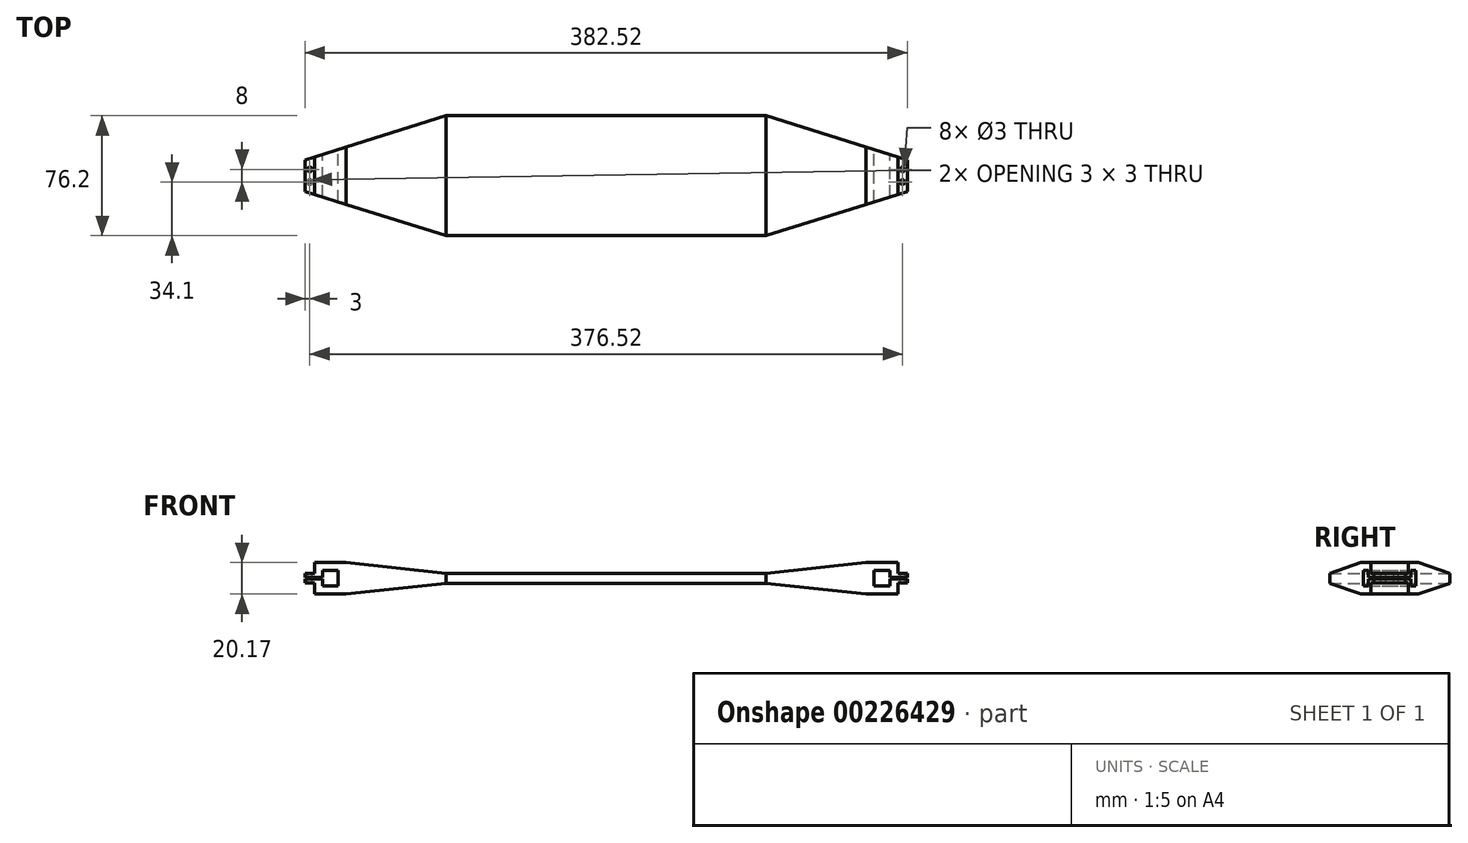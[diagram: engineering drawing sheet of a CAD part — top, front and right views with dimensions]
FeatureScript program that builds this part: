
annotation { "Feature Type Name" : "Feature", "Feature Type Description" : "" }
export const myFeature = defineFeature(function(context is Context, id is Id, definition is map)
    precondition{}
    {
        {
            var Q0;
            Q0=qCreatedBy(makeId("Front.planeOp"),FACE);
            var sketch = newSketch(context, id + "F0", { "sketchPlane" : qUnion([Q0])});
            skLineSegment(sketch, "E0.bottom", {"start": v(-180.18, 8.18) * mm, "end": v(-170.18, 8.18) * mm});
            skLineSegment(sketch, "E0.top", {"start": v(-180.18, -1.83) * mm, "end": v(-170.18, -1.83) * mm});
            skLineSegment(sketch, "E0.right", {"start": v(-170.18, 8.18) * mm, "end": v(-170.18, -1.83) * mm});
            skLineSegment(sketch, "E1.bottom", {"start": v(-165.1, -6.9) * mm, "end": v(-185.26, -6.9) * mm});
            skLineSegment(sketch, "E1.top", {"start": v(-165.1, 13.25) * mm, "end": v(-185.26, 13.25) * mm});
            skLineSegment(sketch, "E1.left", {"start": v(-165.1, -6.9) * mm, "end": v(-165.1, 13.25) * mm});
            skLineSegment(sketch, "E1.right", {"start": v(-185.26, -6.9) * mm, "end": v(-185.26, 2.68) * mm});
            skPoint(sketch, "E1.middle", {"position": v(-175.18, 3.17) * mm});
            skLineSegment(sketch, "E2", {"start": v(-185.26, 13.25) * mm, "end": v(-180.18, 8.17) * mm, "construction": true});
            skLineSegment(sketch, "E3", {"start": v(-170.18, -1.83) * mm, "end": v(-165.1, -6.9) * mm, "construction": true});
            skLineSegment(sketch, "E4", {"start": v(-180.18, -1.82) * mm, "end": v(-185.26, -6.9) * mm, "construction": true});
            skLineSegment(sketch, "E5", {"start": v(-165.1, 6.35) * mm, "end": v(0, 6.35) * mm});
            skLineSegment(sketch, "E6", {"start": v(0, 0) * mm, "end": v(-165.1, 0) * mm});
            skLineSegment(sketch, "E7", {"start": v(-165.1, 13.25) * mm, "end": v(-101.6, 6.35) * mm});
            skLineSegment(sketch, "E8", {"start": v(-101.6, 6.35) * mm, "end": v(-101.6, 0) * mm});
            skLineSegment(sketch, "E9", {"start": v(-101.6, 0) * mm, "end": v(-165.1, -6.9) * mm});
            skLineSegment(sketch, "E10", {"start": v(0, 6.35) * mm, "end": v(0, 0) * mm});
            skLineSegment(sketch, "E11", {"start": v(-180.18, 3.68) * mm, "end": v(-185.26, 3.68) * mm});
            skLineSegment(sketch, "E12", {"start": v(-185.26, 2.68) * mm, "end": v(-180.18, 2.68) * mm});
            skPoint(sketch, "E13", {"position": v(-180.18, 3.17) * mm});
            skLineSegment(sketch, "E14.trimOffspring", {"start": v(-180.18, 2.68) * mm, "end": v(-180.18, -1.83) * mm});
            skLineSegment(sketch, "E15", {"start": v(-180.18, 3.67) * mm, "end": v(-180.18, 8.17) * mm});
            skLineSegment(sketch, "E16.trimOffspring", {"start": v(-185.26, 3.67) * mm, "end": v(-185.26, 13.25) * mm});
            skLineSegment(sketch, "E17", {"start": v(-185.26, 3.68) * mm, "end": v(-191.26, 3.68) * mm});
            skLineSegment(sketch, "E18", {"start": v(-191.26, 3.67) * mm, "end": v(-191.26, 6.22) * mm});
            skLineSegment(sketch, "E19", {"start": v(-191.26, 6.22) * mm, "end": v(-185.26, 6.22) * mm});
            skLineSegment(sketch, "E20", {"start": v(-185.26, 2.68) * mm, "end": v(-191.26, 2.68) * mm});
            skLineSegment(sketch, "E21", {"start": v(-191.26, 2.68) * mm, "end": v(-191.26, 0.13) * mm});
            skLineSegment(sketch, "E22", {"start": v(-191.26, 0.13) * mm, "end": v(-185.26, 0.13) * mm});
            skLineSegment(sketch, "E23.MirrorCS", {"start": v(180.18, 3.67) * mm, "end": v(180.18, 8.17) * mm});
            skLineSegment(sketch, "E24.MirrorCS", {"start": v(180.18, 2.68) * mm, "end": v(180.18, -1.83) * mm});
            skLineSegment(sketch, "E25.MirrorCS", {"start": v(191.26, 3.67) * mm, "end": v(191.26, 6.22) * mm});
            skLineSegment(sketch, "E26.MirrorCS", {"start": v(191.26, 2.67) * mm, "end": v(191.26, 0.13) * mm});
            skLineSegment(sketch, "E27.MirrorCS", {"start": v(180.18, 8.18) * mm, "end": v(170.18, 8.18) * mm});
            skLineSegment(sketch, "E28.MirrorCS", {"start": v(180.18, 3.68) * mm, "end": v(185.26, 3.68) * mm});
            skLineSegment(sketch, "E29.MirrorCS", {"start": v(185.26, 2.68) * mm, "end": v(180.18, 2.68) * mm});
            skLineSegment(sketch, "E30.MirrorCS", {"start": v(180.18, -1.82) * mm, "end": v(185.26, -6.9) * mm, "construction": true});
            skLineSegment(sketch, "E31.MirrorCS", {"start": v(185.26, 13.25) * mm, "end": v(180.18, 8.17) * mm, "construction": true});
            skLineSegment(sketch, "E32.MirrorCS", {"start": v(191.26, 6.22) * mm, "end": v(185.26, 6.22) * mm});
            skLineSegment(sketch, "E33.MirrorCS", {"start": v(185.26, -6.9) * mm, "end": v(185.26, 2.68) * mm});
            skLineSegment(sketch, "E34.MirrorCS", {"start": v(191.26, 0.13) * mm, "end": v(185.26, 0.13) * mm});
            skLineSegment(sketch, "E35.MirrorCS", {"start": v(170.18, 8.18) * mm, "end": v(170.18, -1.82) * mm});
            skLineSegment(sketch, "E36.MirrorCS", {"start": v(0, 0) * mm, "end": v(165.1, 0) * mm});
            skLineSegment(sketch, "E37.MirrorCS", {"start": v(180.18, -1.83) * mm, "end": v(170.18, -1.83) * mm});
            skPoint(sketch, "E38.MirrorP", {"position": v(175.18, 3.17) * mm});
            skPoint(sketch, "E39.MirrorP", {"position": v(180.18, 3.17) * mm});
            skLineSegment(sketch, "E40.MirrorCS", {"start": v(101.6, 6.35) * mm, "end": v(101.6, 0) * mm});
            skLineSegment(sketch, "E41.MirrorCS", {"start": v(165.1, 13.25) * mm, "end": v(185.26, 13.25) * mm});
            skLineSegment(sketch, "E42.MirrorCS", {"start": v(165.1, -6.9) * mm, "end": v(185.26, -6.9) * mm});
            skLineSegment(sketch, "E43.MirrorCS", {"start": v(185.26, 3.67) * mm, "end": v(185.26, 13.25) * mm});
            skLineSegment(sketch, "E44.MirrorCS", {"start": v(165.1, -6.9) * mm, "end": v(165.1, 13.25) * mm});
            skLineSegment(sketch, "E45.MirrorCS", {"start": v(165.1, 6.35) * mm, "end": v(0, 6.35) * mm});
            skLineSegment(sketch, "E46.MirrorCS", {"start": v(185.26, 3.68) * mm, "end": v(191.26, 3.68) * mm});
            skLineSegment(sketch, "E47.MirrorCS", {"start": v(101.6, 0) * mm, "end": v(165.1, -6.9) * mm});
            skLineSegment(sketch, "E48.MirrorCS", {"start": v(185.26, 2.68) * mm, "end": v(191.26, 2.68) * mm});
            skLineSegment(sketch, "E49.MirrorCS", {"start": v(170.18, -1.83) * mm, "end": v(165.1, -6.9) * mm, "construction": true});
            skLineSegment(sketch, "E50.MirrorCS", {"start": v(165.1, 13.25) * mm, "end": v(101.6, 6.35) * mm});
            skSolve(sketch);
        }
        {
            var Q0;
            Q0=qSketchRegion(id+"F0",true);
            extrude(context, id + "F1", {"entities" : qUnion([Q0]), "depth" : 76.2 * mm, "offsetDistance" : 25.4 * mm});
        }
        {
            var Q0;
            Q0=makeQuery(id+"F1.opExtrude","SWEPT_FACE",FACE,{"disambiguationData":[OSD([sQuery(id+"F0.wireOp",EDGE,"E5")])]});
            var sketch = newSketch(context, id + "F2", { "sketchPlane" : qUnion([Q0])});
            skLineSegment(sketch, "E51.bottom", {"start": v(-101.6, 0) * mm, "end": v(101.6, 0) * mm, "construction": true});
            skLineSegment(sketch, "E51.top", {"start": v(-101.6, -76.2) * mm, "end": v(101.6, -76.2) * mm, "construction": true});
            skLineSegment(sketch, "E51.left", {"start": v(-101.6, 0) * mm, "end": v(-101.6, -76.2) * mm, "construction": true});
            skLineSegment(sketch, "E51.right", {"start": v(101.6, 0) * mm, "end": v(101.6, -76.2) * mm, "construction": true});
            skLineSegment(sketch, "E52.bottom", {"start": v(-26, -12.1) * mm, "end": v(26, -12.1) * mm, "construction": true});
            skLineSegment(sketch, "E52.top", {"start": v(-26, -64.1) * mm, "end": v(26, -64.1) * mm, "construction": true});
            skLineSegment(sketch, "E52.left", {"start": v(-26, -12.1) * mm, "end": v(-26, -64.1) * mm, "construction": true});
            skLineSegment(sketch, "E52.right", {"start": v(26, -12.1) * mm, "end": v(26, -64.1) * mm, "construction": true});
            skLineSegment(sketch, "E53.bottom", {"start": v(-38.1, -9.52) * mm, "end": v(38.1, -9.52) * mm, "construction": true});
            skLineSegment(sketch, "E53.top", {"start": v(-38.1, -66.68) * mm, "end": v(38.1, -66.68) * mm, "construction": true});
            skLineSegment(sketch, "E53.left", {"start": v(-38.1, -9.52) * mm, "end": v(-38.1, -66.67) * mm, "construction": true});
            skLineSegment(sketch, "E53.right", {"start": v(38.1, -9.52) * mm, "end": v(38.1, -66.67) * mm, "construction": true});
            skLineSegment(sketch, "E54", {"start": v(0, -12.1) * mm, "end": v(0, 0) * mm, "construction": true});
            skLineSegment(sketch, "E55", {"start": v(26, -38.1) * mm, "end": v(101.6, -38.1) * mm, "construction": true});
            skLineSegment(sketch, "E56", {"start": v(0, -9.52) * mm, "end": v(0, 0) * mm});
            skLineSegment(sketch, "E57", {"start": v(38.1, -38.1) * mm, "end": v(101.6, -38.1) * mm, "construction": true});
            skCircle(sketch, "E58", {"center": v(-38.1, -9.52) * mm, "radius": 4.45 * mm});
            skCircle(sketch, "E59", {"center": v(38.1, -9.52) * mm, "radius": 4.45 * mm});
            skCircle(sketch, "E60", {"center": v(38.1, -66.67) * mm, "radius": 4.45 * mm});
            skCircle(sketch, "E61", {"center": v(-38.1, -66.67) * mm, "radius": 4.45 * mm});
            skCircle(sketch, "E62", {"center": v(-23, -15.1) * mm, "radius": 1.59 * mm});
            skCircle(sketch, "E63", {"center": v(23, -61.1) * mm, "radius": 1.59 * mm});
            skLineSegment(sketch, "E64", {"start": v(-23, -12.1) * mm, "end": v(-23, -64.1) * mm, "construction": true});
            skLineSegment(sketch, "E65", {"start": v(-26, -61.1) * mm, "end": v(26, -61.1) * mm, "construction": true});
            skLineSegment(sketch, "E66", {"start": v(23, -64.1) * mm, "end": v(23, -12.1) * mm, "construction": true});
            skLineSegment(sketch, "E67", {"start": v(26, -15.1) * mm, "end": v(-26, -15.1) * mm, "construction": true});
            skCircle(sketch, "E68", {"center": v(23, -15.1) * mm, "radius": 1.59 * mm});
            skCircle(sketch, "E69", {"center": v(-23, -61.1) * mm, "radius": 1.59 * mm});
            skSolve(sketch);
        }
        {
            var Q0;
            Q0=qSketchRegion(id+"F2",true);
            extrude(context, id + "F3", {"entities" : qUnion([Q0]), "operationType" : NewBodyOperationType.REMOVE, "oppositeDirection" : true, "depth" : 25.4 * mm, "offsetDistance" : 25.4 * mm});
        }
        {
            var Q0;
            Q0=makeQuery(id+"F1.opExtrude","SWEPT_FACE",FACE,{"disambiguationData":[OSD([sQuery(id+"F0.wireOp",EDGE,"E19")])]});
            var sketch = newSketch(context, id + "F4", { "sketchPlane" : qUnion([Q0])});
            skCircle(sketch, "E70", {"center": v(-188.26, -34.1) * mm, "radius": 1.5 * mm});
            skPoint(sketch, "E70.centerSnap0", {"position": v(-188.26, 0) * mm});
            skCircle(sketch, "E71", {"center": v(-188.26, -42.1) * mm, "radius": 1.5 * mm});
            skPoint(sketch, "E71.centerSnap0", {"position": v(-188.26, -76.2) * mm});
            skLineSegment(sketch, "E72", {"start": v(0, 0) * mm, "end": v(0, -76.82) * mm});
            skCircle(sketch, "E73.MirrorC", {"center": v(188.26, -42.1) * mm, "radius": 1.5 * mm});
            skCircle(sketch, "E74.MirrorC", {"center": v(188.26, -34.1) * mm, "radius": 1.5 * mm});
            skPoint(sketch, "E75.MirrorP", {"position": v(188.26, -76.2) * mm});
            skSolve(sketch);
        }
        {
            var Q0;
            Q0=qSketchRegion(id+"F4",true);
            extrude(context, id + "F5", {"entities" : qUnion([Q0]), "operationType" : NewBodyOperationType.REMOVE, "endBound" : BoundingType.THROUGH_ALL, "oppositeDirection" : true, "depth" : 25 * mm, "offsetDistance" : 25 * mm});
        }
        {
            var Q0;
            Q0=makeQuery(id+"F1.opExtrude","SWEPT_FACE",FACE,{"disambiguationData":[OSD([sQuery(id+"F0.wireOp",EDGE,"E1.top")])]});
            var sketch = newSketch(context, id + "F6", { "sketchPlane" : qUnion([Q0])});
            skPoint(sketch, "E76.0", {"position": v(-101.6, 0) * mm});
            skLineSegment(sketch, "E77", {"start": v(-101.6, 0) * mm, "end": v(-191.26, -28.1) * mm});
            skLineSegment(sketch, "E78.0", {"start": v(-191.26, -76.2) * mm, "end": v(-191.26, 0) * mm});
            skPoint(sketch, "E79", {"position": v(-191.26, -38.1) * mm});
            skLineSegment(sketch, "E80.MirrorCS", {"start": v(101.6, 0) * mm, "end": v(191.26, -28.1) * mm});
            skLineSegment(sketch, "E81", {"start": v(-191.26, -38.1) * mm, "end": v(196.24, -38.1) * mm});
            skLineSegment(sketch, "E82.MirrorCS", {"start": v(-101.6, -76.2) * mm, "end": v(-191.26, -48.1) * mm});
            skLineSegment(sketch, "E83.MirrorCS", {"start": v(101.6, -76.2) * mm, "end": v(191.26, -48.1) * mm});
            skLineSegment(sketch, "E84", {"start": v(-101.6, 0) * mm, "end": v(-191.26, 0) * mm});
            skLineSegment(sketch, "E85", {"start": v(-101.6, -76.2) * mm, "end": v(-191.26, -76.2) * mm});
            skLineSegment(sketch, "E86", {"start": v(101.6, -76.2) * mm, "end": v(191.26, -76.2) * mm});
            skLineSegment(sketch, "E87", {"start": v(191.26, -76.2) * mm, "end": v(191.26, -48.1) * mm});
            skLineSegment(sketch, "E88", {"start": v(191.26, -28.1) * mm, "end": v(191.26, 0) * mm});
            skLineSegment(sketch, "E89", {"start": v(191.26, 0) * mm, "end": v(101.6, 0) * mm});
            skSolve(sketch);
        }
        {
            var Q0;
            {var subQ0=sQuery(id+"F6.wireOp",EDGE,"E84");var subQ1=sQuery(id+"F6.wireOp",EDGE,"E77");var subQ2=makeQuery(id+"F6.imprint","INTERSECT",VERTEX,{"derivedFrom":[subQ1,subQ0]});Q0=makeQuery(id+"F6.imprint","IMPRINT",FACE,{"disambiguationData":[TD([[makeQuery(id+"F6.imprint","IMPRINT",EDGE,{"disambiguationData":[TD([[subQ2,-1.0]])],"derivedFrom":subQ1}),-1.0]])]});}
            var Q1;
            {var subQ0=sQuery(id+"F6.wireOp",EDGE,"E77");var subQ1=sQuery(id+"F0.wireOp",EDGE,"E1.top");var subQ4=makeQuery(id+"F1.opExtrude","SWEPT_EDGE",EDGE,{"disambiguationData":[OSD([subQ1,sQuery(id+"F0.wireOp",EDGE,"E16.trimOffspring")])]});var subQ5=makeQuery(id+"F6.imprint","INTERSECT",VERTEX,{"derivedFrom":[subQ4,subQ0]});Q1=makeQuery(id+"F6.imprint","IMPRINT",FACE,{"disambiguationData":[TD([[makeQuery(id+"F6.imprint","IMPRINT",EDGE,{"disambiguationData":[TD([[subQ5,1.0]])],"derivedFrom":subQ0}),-1.0]])]});}
            var Q2;
            {var subQ0=sQuery(id+"F6.wireOp",EDGE,"E78.0");var subQ1=sQuery(id+"F6.wireOp",EDGE,"E77");var subQ2=makeQuery(id+"F6.imprint","INTERSECT",VERTEX,{"derivedFrom":[subQ1,subQ0]});Q2=makeQuery(id+"F6.imprint","IMPRINT",FACE,{"disambiguationData":[TD([[makeQuery(id+"F6.imprint","IMPRINT",EDGE,{"disambiguationData":[TD([[subQ2,-1.0]])],"derivedFrom":subQ0}),-1.0]])]});}
            var Q3;
            {var subQ0=sQuery(id+"F6.wireOp",EDGE,"E85");var subQ1=sQuery(id+"F6.wireOp",EDGE,"E78.0");var subQ2=makeQuery(id+"F6.imprint","INTERSECT",VERTEX,{"derivedFrom":[subQ1,subQ0]});Q3=makeQuery(id+"F6.imprint","IMPRINT",FACE,{"disambiguationData":[TD([[makeQuery(id+"F6.imprint","IMPRINT",EDGE,{"disambiguationData":[TD([[subQ2,-1.0]])],"derivedFrom":subQ1}),-1.0]])]});}
            var Q4;
            {var subQ0=sQuery(id+"F6.wireOp",EDGE,"E82.MirrorCS");var subQ1=sQuery(id+"F0.wireOp",EDGE,"E1.top");var subQ4=makeQuery(id+"F1.opExtrude","SWEPT_EDGE",EDGE,{"disambiguationData":[OSD([subQ1,sQuery(id+"F0.wireOp",EDGE,"E16.trimOffspring")])]});var subQ5=makeQuery(id+"F6.imprint","INTERSECT",VERTEX,{"derivedFrom":[subQ4,subQ0]});Q4=makeQuery(id+"F6.imprint","IMPRINT",FACE,{"disambiguationData":[TD([[makeQuery(id+"F6.imprint","IMPRINT",EDGE,{"disambiguationData":[TD([[subQ5,1.0]])],"derivedFrom":subQ0}),1.0]])]});}
            var Q5;
            {var subQ0=sQuery(id+"F6.wireOp",EDGE,"E85");var subQ1=sQuery(id+"F6.wireOp",EDGE,"E82.MirrorCS");var subQ2=makeQuery(id+"F6.imprint","INTERSECT",VERTEX,{"derivedFrom":[subQ1,subQ0]});Q5=makeQuery(id+"F6.imprint","IMPRINT",FACE,{"disambiguationData":[TD([[makeQuery(id+"F6.imprint","IMPRINT",EDGE,{"disambiguationData":[TD([[subQ2,-1.0]])],"derivedFrom":subQ1}),1.0]])]});}
            var Q6;
            Q6=makeQuery(id+"F6.imprint","IMPRINT",FACE,{"disambiguationData":[TD([[makeQuery(id+"F6.imprint","IMPRINT",EDGE,{"derivedFrom":sQuery(id+"F6.wireOp",EDGE,"E83.MirrorCS")}),-1.0]])]});
            var Q7;
            Q7=makeQuery(id+"F6.imprint","IMPRINT",FACE,{"disambiguationData":[TD([[makeQuery(id+"F6.imprint","IMPRINT",EDGE,{"derivedFrom":sQuery(id+"F6.wireOp",EDGE,"E80.MirrorCS")}),1.0]])]});
            extrude(context, id + "F7", {"entities" : qUnion([Q0, Q1, Q2, Q3, Q4, Q5, Q6, Q7]), "operationType" : NewBodyOperationType.REMOVE, "endBound" : BoundingType.THROUGH_ALL, "oppositeDirection" : true, "depth" : 25 * mm, "offsetDistance" : 25 * mm});
        }
        {
            var Q0;
            Q0=makeQuery(id+"F1.opExtrude","SWEPT_FACE",FACE,{"disambiguationData":[OSD([sQuery(id+"F0.wireOp",EDGE,"E6"),sQuery(id+"F0.wireOp",EDGE,"E36.MirrorCS")])]});
            var sketch = newSketch(context, id + "F8", { "sketchPlane" : qUnion([Q0])});
            skCircle(sketch, "E90.0", {"center": v(-38.1, 66.67) * mm, "radius": 4.45 * mm});
            skCircle(sketch, "E90.1", {"center": v(-38.1, 9.52) * mm, "radius": 4.45 * mm});
            skCircle(sketch, "E90.2", {"center": v(-23, 15.1) * mm, "radius": 1.59 * mm});
            skCircle(sketch, "E90.3", {"center": v(38.1, 9.52) * mm, "radius": 4.45 * mm});
            skCircle(sketch, "E90.4", {"center": v(38.1, 66.67) * mm, "radius": 4.45 * mm});
            skCircle(sketch, "E90.5", {"center": v(23, 61.1) * mm, "radius": 1.59 * mm});
            skCircle(sketch, "E90.6", {"center": v(-23, 61.1) * mm, "radius": 1.59 * mm});
            skCircle(sketch, "E90.7", {"center": v(23, 15.1) * mm, "radius": 1.59 * mm});
            skSolve(sketch);
        }
        {
            var Q0;
            Q0 = qSketchRegion(id + "F8", true);
            var Q1;
            Q1=makeQuery(id+"F1.opExtrude","SWEPT_FACE",FACE,{"disambiguationData":[OSD([sQuery(id+"F0.wireOp",EDGE,"E5"),sQuery(id+"F0.wireOp",EDGE,"E45.MirrorCS")])]});
            extrude(context, id + "F9", {"entities" : qUnion([Q0]), "operationType" : NewBodyOperationType.ADD, "endBound" : BoundingType.UP_TO_SURFACE, "oppositeDirection" : true, "depth" : 25 * mm, "endBoundEntityFace" : qUnion([Q1]), "offsetDistance" : 25 * mm});
        }
    });
